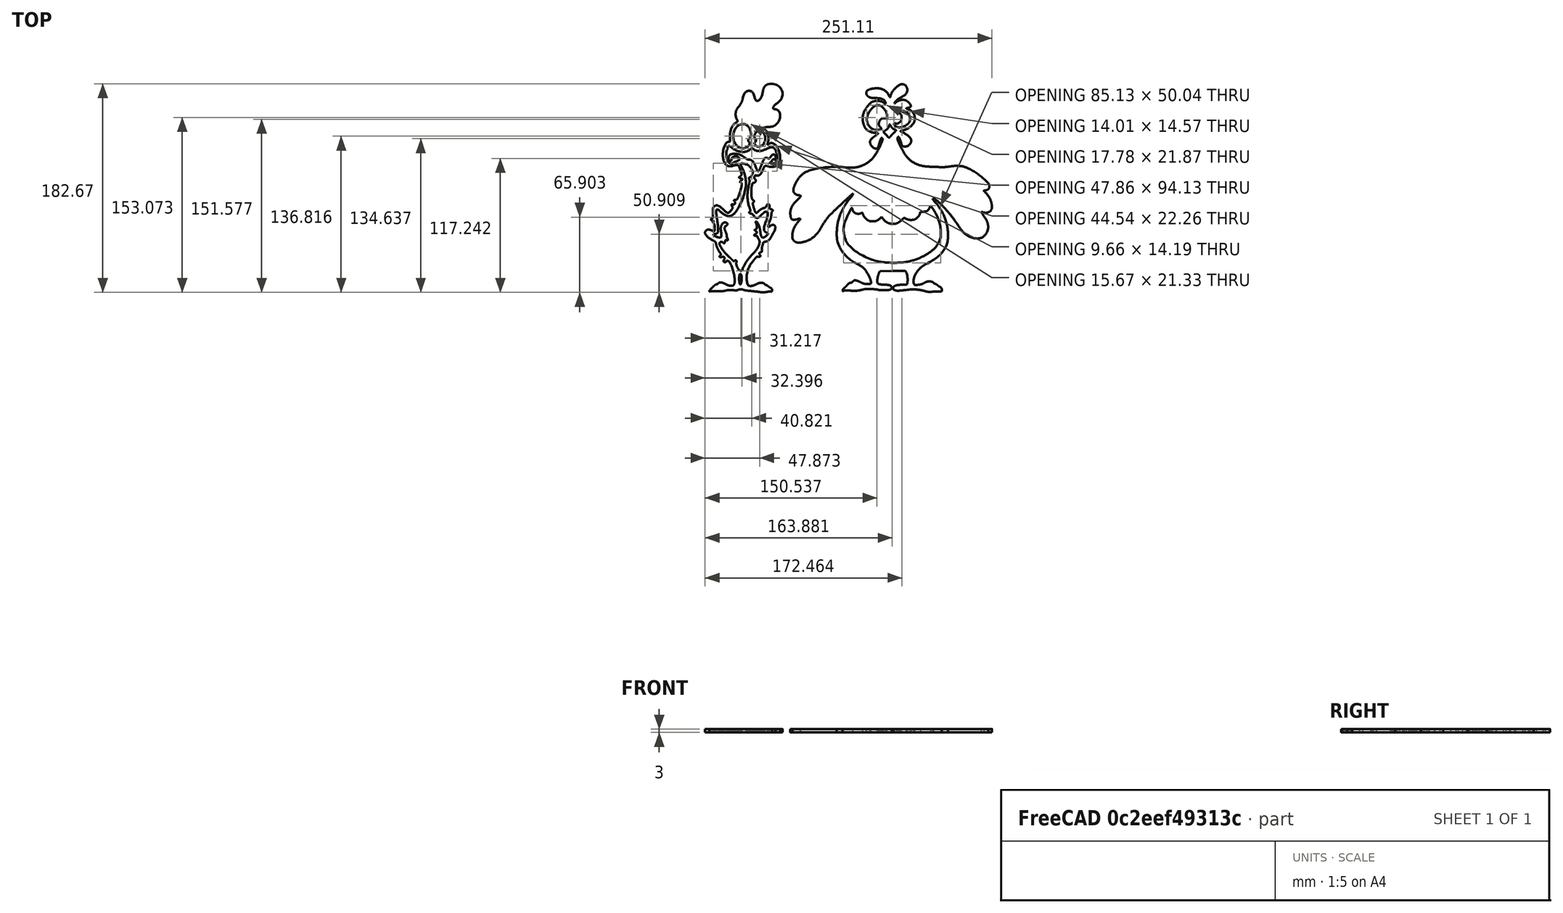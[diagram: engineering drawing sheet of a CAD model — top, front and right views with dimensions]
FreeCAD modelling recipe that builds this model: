
FCSTD DOCUMENT  (FreeCAD 1.1R44874 (Git))
Label: obraz
License: All rights reserved
LicenseURL: https://en.wikipedia.org/wiki/All_rights_reserved
objects: Part::Feature×2, Part::Extrusion×2, PartDesign::Body×1, App::Point×1
note: 5 computed .brp shape members not serialized (recipe doc carries the construction recipe); baked Part::Feature solids carry a one-line shape summary decoded from their .brp

FEATURE [PartDesign::Body] Body
  AllowCompound = false
  Origin = -> Origin
FEATURE [App::Point] Origin001
  Role = Origin
FEATURE [Part::Feature] path882
  shape: bbox 176.9 x 181.9 x 2e-07 mm, 1 faces, 0 solids (baked)
FEATURE [Part::Extrusion] Extrude  label="slepice"
  Base = -> path882
  Dir = (0,0,-1)
  DirMode = 2
  FaceMakerClass = Part::FaceMakerBullseye
  FaceMakerMode = 3
  InnerWireTaper = 0
  LengthFwd = 3
  LengthRev = 0
  Placement = pos=(15,48,0) rot=(0,0,1;0rad)
  Solid = false
  Symmetric = false
FEATURE [Part::Feature] path1441
  shape: bbox 70.1 x 184.4 x 2e-07 mm, 1 faces, 0 solids (baked)
FEATURE [Part::Extrusion] Extrude001  label="kohout"
  Base = -> path1441
  Dir = (0,0,-1)
  DirMode = 2
  FaceMakerClass = Part::FaceMakerBullseye
  FaceMakerMode = 3
  InnerWireTaper = 0
  LengthFwd = 3
  LengthRev = 0
  Placement = pos=(-108,39,0) rot=(0,0,1;0rad)
  Solid = false
  Symmetric = false
